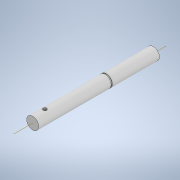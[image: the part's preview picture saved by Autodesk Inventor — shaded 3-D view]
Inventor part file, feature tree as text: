
AUTODESK INVENTOR PART (.ipt)
format: ipt  version: 2022 (Build 260153000, 153)  size: 131,072 bytes
history: native  units: in
note: dims shown in document units (in); Inventor stores cm internally (conversion verified against a paired STEP export)
features: sketch x3, other x2, extrude x1, hole x1, revolve x1
ambient origin geometry x8: Origin, YZ Plane, XZ Plane, XY Plane, X Axis, Y Axis, Z Axis, Center Point
bodies: Solid1 (feature_tree)
feature tree (8):
  other  "Shaft"
  extrude  "Extrusion1"  Depth=3.937in TaperAngle=0.0deg
  hole  "Hole1"  [1 undecoded]
  other  "Work Axis1"
  revolve  "Revolution2"  [1 undecoded]
  sketch  "Sketch3"  dims[d0=0.3937in d1=3.937in d2=0.0in]
  sketch  "Sketch4"  dims[d3=0.1181in]
  sketch  "Sketch14"  dims[d4=0.1181in d5=0.146in d6=0.119in d7=0.0787in d8=0.5635in d9=0.3937in d10=0.8108in d11=0.3937in d22=2.3622in d23=0.0157in d24=0.0394in d25=360.0deg d12=0.0394in d13=0.0394in d14=0.0059in d15=0.0098in d16=0.0148in d17=0.5635in d18=0.0295in d19=0.8108in d20=0.0025in d21=0.0295in]
note: 2 required parameter values undecoded (feature->parameter linkage not recoverable at this tier; creation-order binding heuristic only, values carry confidence <= 0.55)